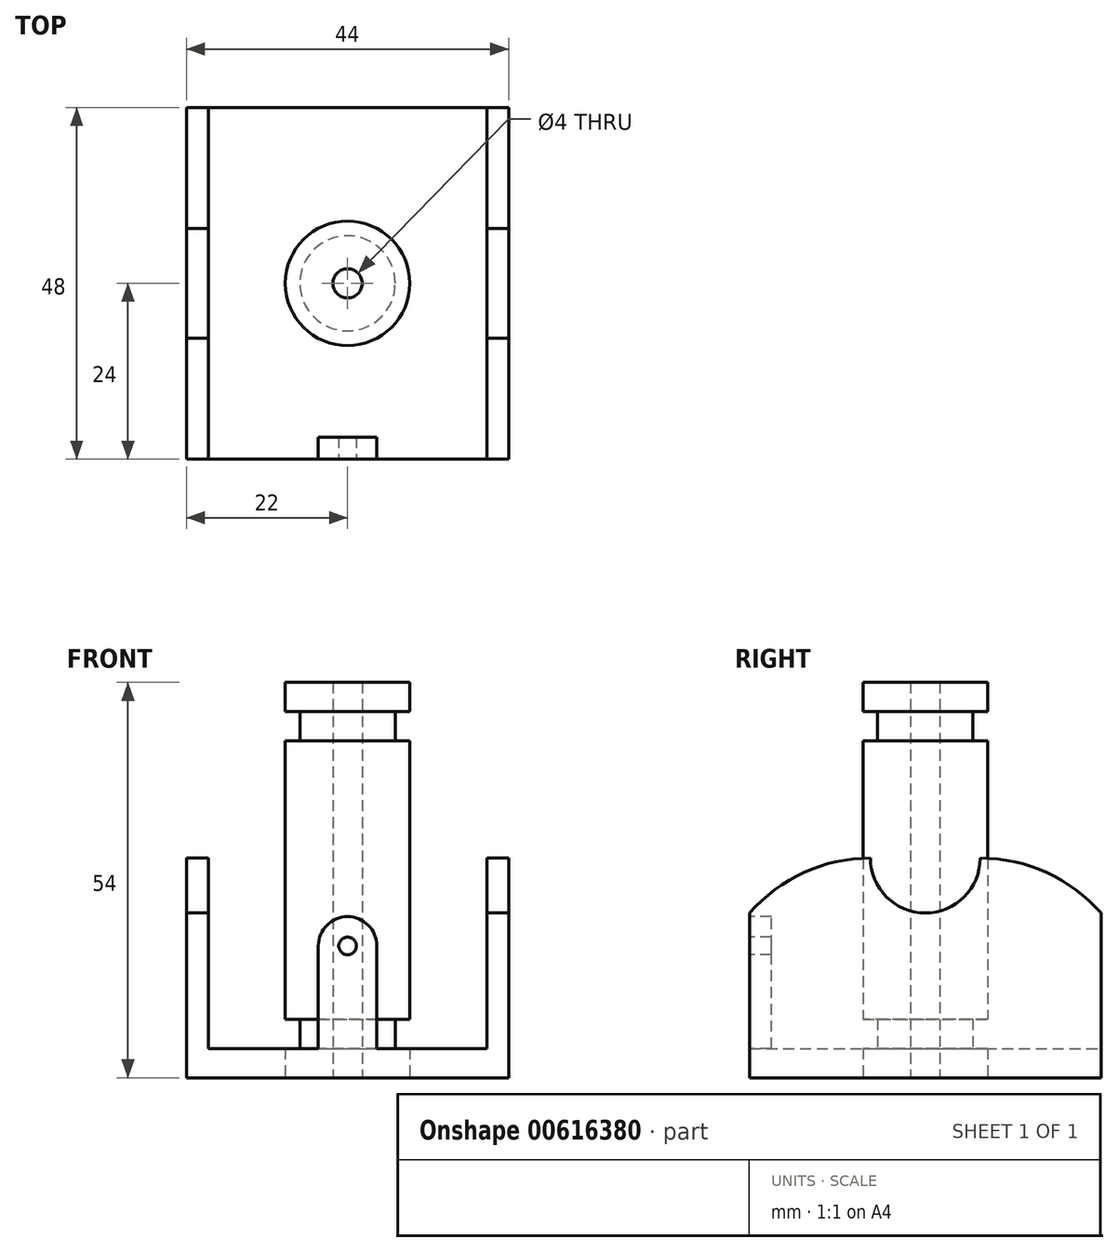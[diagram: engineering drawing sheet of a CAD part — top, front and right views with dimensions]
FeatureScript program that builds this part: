
annotation { "Feature Type Name" : "Feature", "Feature Type Description" : "" }
export const myFeature = defineFeature(function(context is Context, id is Id, definition is map)
    precondition{}
    {
        {
            assignVariable(context, id + "F0", {"name" : "GrooveWidth", "anyValue" : 4 * mm});
        }
        {
            var Q0;
            Q0=qCreatedBy(makeId("Right.planeOp"),FACE);
            var sketch = newSketch(context, id + "F1", { "sketchPlane" : qUnion([Q0])});
            skLineSegment(sketch, "E0", {"start": v(2, 0) * mm, "end": v(8.5, 0) * mm});
            skLineSegment(sketch, "E1", {"start": v(8.5, 0) * mm, "end": v(8.5, 4) * mm});
            skLineSegment(sketch, "E2", {"start": v(8.5, 4) * mm, "end": v(6.5, 4) * mm});
            skLineSegment(sketch, "E3", {"start": v(6.5, 4) * mm, "end": v(6.5, 8) * mm});
            skLineSegment(sketch, "E4", {"start": v(6.5, 8) * mm, "end": v(8.5, 8) * mm});
            skLineSegment(sketch, "E5", {"start": v(8.5, 8) * mm, "end": v(8.5, 46) * mm});
            skLineSegment(sketch, "E6", {"start": v(8.5, 46) * mm, "end": v(6.5, 46) * mm});
            skLineSegment(sketch, "E7", {"start": v(6.5, 46) * mm, "end": v(6.5, 50) * mm});
            skLineSegment(sketch, "E8", {"start": v(6.5, 50) * mm, "end": v(8.5, 50) * mm});
            skLineSegment(sketch, "E9", {"start": v(8.5, 50) * mm, "end": v(8.5, 54) * mm});
            skLineSegment(sketch, "E10", {"start": v(8.5, 54) * mm, "end": v(2, 54) * mm});
            skLineSegment(sketch, "E11", {"start": v(2, 54) * mm, "end": v(2, 0) * mm});
            skLineSegment(sketch, "E12", {"start": v(0, 0) * mm, "end": v(0, 13.08) * mm, "construction": true});
            skPoint(sketch, "E13", {"position": v(6.5, 0) * mm});
            skSolve(sketch);
        }
        {
            var Q0;
            Q0=makeQuery(id+"F1.imprint","IMPRINT",FACE,{"disambiguationData":[TD([[makeQuery(id+"F1.imprint","IMPRINT",EDGE,{"derivedFrom":sQuery(id+"F1.wireOp",EDGE,"E0")}),1.0]])]});
            var Q1;
            Q1=sQuery(id+"F1.wireOp",EDGE,"E12");
            revolve(context, id + "F2", {"entities" : qUnion([Q0]), "axis" : qUnion([Q1]), "revolveType" : RevolveType.FULL});
        }
        {
            assignVariable(context, id + "F3", {"name" : "BottomThickness", "anyValue" : 4 * mm});
        }
        {
            assignVariable(context, id + "F4", {"name" : "WallWidth", "anyValue" : getVariable(context, 'GrooveWidth') - 1 * mm});
        }
        {
            var Q0;
            Q0=qCreatedBy(makeId("Top.planeOp"),FACE);
            var sketch = newSketch(context, id + "F5", { "sketchPlane" : qUnion([Q0])});
            skPoint(sketch, "E14.0", {"position": v(-26.4, -28.56) * mm});
            skPoint(sketch, "E15.0", {"position": v(12, -28.56) * mm});
            skLineSegment(sketch, "E16.bottom", {"start": v(-19, -24) * mm, "end": v(19, -24) * mm});
            skLineSegment(sketch, "E16.top", {"start": v(-19, 24) * mm, "end": v(19, 24) * mm});
            skLineSegment(sketch, "E16.left", {"start": v(-19, -24) * mm, "end": v(-19, 24) * mm});
            skLineSegment(sketch, "E16.right", {"start": v(19, -24) * mm, "end": v(19, 24) * mm});
            skLineSegment(sketch, "E17", {"start": v(0, 24) * mm, "end": v(0, 21.41) * mm, "construction": true});
            skPoint(sketch, "E18", {"position": v(-19, 0) * mm});
            skSolve(sketch);
        }
        {
            var Q0;
            Q0 = qSketchRegion(id + "F5", true);
            extrude(context, id + "F6", {"entities" : qUnion([Q0]), "depth" : getVariable(context, 'BottomThickness'), "offsetDistance" : 25 * mm});
        }
        {
            var Q0;
            Q0=makeQuery(id+"F6.opExtrude","CAP_EDGE",EDGE,{"disambiguationData":[OSD([sQuery(id+"F5.wireOp",EDGE,"E16.left")])],"isStart":false});
            cPlane(context, id + "F7", {"entities" : qUnion([Q0]), "cplaneType" : CPlaneType.LINE_ANGLE, "offset" : 25 * mm, "angle" : 90 * degree, "width" : 150 * mm, "height" : 150 * mm});
        }
        {
            var Q0;
            Q0=qCreatedBy(id+"F7.planeOp",FACE);
            var sketch = newSketch(context, id + "F8", { "sketchPlane" : qUnion([Q0])});
            skPoint(sketch, "E19", {"position": v(0, 0) * mm});
            skArc(sketch, "E20", {"start": v(-7.5, 30) * mm, "mid": v(-5.3, 24.7) * mm, "end": v(0, 22.5) * mm});
            skLineSegment(sketch, "E21", {"start": v(0, 22.5) * mm, "end": v(0, 0) * mm});
            skPoint(sketch, "E22.0", {"position": v(-24, 0) * mm});
            skLineSegment(sketch, "E23", {"start": v(0, 0) * mm, "end": v(-24, 0) * mm});
            skLineSegment(sketch, "E24", {"start": v(-24, 0) * mm, "end": v(-24, 22.5) * mm});
            skArc(sketch, "E25.MirrorCS", {"start": v(7.5, 30) * mm, "mid": v(5.3, 24.7) * mm, "end": v(0, 22.5) * mm});
            skLineSegment(sketch, "E26.MirrorCS", {"start": v(24, 0) * mm, "end": v(24, 22.5) * mm});
            skLineSegment(sketch, "E27.MirrorCS", {"start": v(0, 0) * mm, "end": v(24, 0) * mm});
            skArc(sketch, "E28", {"start": v(-7.5, 30) * mm, "mid": v(-16.56, 28.04) * mm, "end": v(-24, 22.5) * mm});
            skLineSegment(sketch, "E29", {"start": v(-7.5, 30) * mm, "end": v(-13.52, 30) * mm, "construction": true});
            skArc(sketch, "E30.MirrorCS", {"start": v(7.5, 30) * mm, "mid": v(16.56, 28.04) * mm, "end": v(24, 22.5) * mm});
            skSolve(sketch);
        }
        {
            var Q0;
            Q0 = qSketchRegion(id + "F8", true);
            extrude(context, id + "F9", {"entities" : qUnion([Q0]), "oppositeDirection" : true, "depth" : getVariable(context, 'WallWidth'), "offsetDistance" : 25 * mm});
        }
        {
            var Q0;
            Q0=makeQuery(id+"F9.opExtrude","SWEPT_BODY",BODY,{"disambiguationData":[OSD([sQuery(id+"F8.wireOp",EDGE,"9JeovSxn-ePik-cWq1-eT7D-6XzTEuUeVBdg"),sQuery(id+"F8.wireOp",EDGE,"nZFAqrn0-QC6r-7o5s-tL9m-rpbUFwPPu9rI"),sQuery(id+"F8.wireOp",EDGE,"E20"),sQuery(id+"F8.wireOp",EDGE,"1nsFa8vr-KDjd-aLEX-kK5k-B4Ic1zkwJqWQ"),sQuery(id+"F8.wireOp",EDGE,"c7bf17d6-1071-40d7-9fd2-1aabbd4c07420.MirrorCS"),sQuery(id+"F8.wireOp",EDGE,"afbb585f-af68-4d87-9d94-643ccf565ece0.MirrorCS"),sQuery(id+"F8.wireOp",EDGE,"e3347bec-d21a-411a-bcd6-7515ae25ba6f0.MirrorCS"),sQuery(id+"F8.wireOp",EDGE,"d4b9c155-9cf0-42d5-a583-9f42b9c8f3040.MirrorCS")])]});
            var Q1;
            Q1=qCreatedBy(makeId("Right.planeOp"),FACE);
            mirror(context, id + "F10", {"operationType" : NewBodyOperationType.ADD, "entities" : qUnion([Q0]), "mirrorPlane" : qUnion([Q1])});
        }
        {
            assignVariable(context, id + "F11", {"name" : "SolderThickness", "anyValue" : 3 * mm});
        }
        {
            var Q0;
            Q0=makeQuery(id+"F6.opExtrude","SWEPT_FACE",FACE,{"disambiguationData":[OSD([sQuery(id+"F5.wireOp",EDGE,"E16.bottom")])]});
            var sketch = newSketch(context, id + "F12", { "sketchPlane" : qUnion([Q0])});
            skLineSegment(sketch, "E31", {"start": v(-4, 4) * mm, "end": v(4, 4) * mm});
            skLineSegment(sketch, "E32", {"start": v(4, 4) * mm, "end": v(4, 18) * mm});
            skLineSegment(sketch, "E33", {"start": v(-4, 18) * mm, "end": v(-4, 4) * mm});
            skPoint(sketch, "E34", {"position": v(0, 4) * mm});
            skArc(sketch, "E35", {"start": v(4, 18) * mm, "mid": v(0, 22) * mm, "end": v(-4, 18) * mm});
            skCircle(sketch, "E36", {"center": v(0, 18) * mm, "radius": 1.2 * mm});
            skLineSegment(sketch, "E37.0", {"start": v(-19, 4) * mm, "end": v(19, 4) * mm, "construction": true});
            skSolve(sketch);
        }
        {
            var Q0;
            Q0=makeQuery(id+"F12.imprint","IMPRINT",FACE,{"disambiguationData":[TD([[makeQuery(id+"F12.imprint","IMPRINT",EDGE,{"derivedFrom":sQuery(id+"F12.wireOp",EDGE,"E31")}),1.0]])]});
            extrude(context, id + "F13", {"entities" : qUnion([Q0]), "operationType" : NewBodyOperationType.ADD, "oppositeDirection" : true, "depth" : getVariable(context, 'SolderThickness'), "offsetDistance" : 25 * mm});
        }
    });
